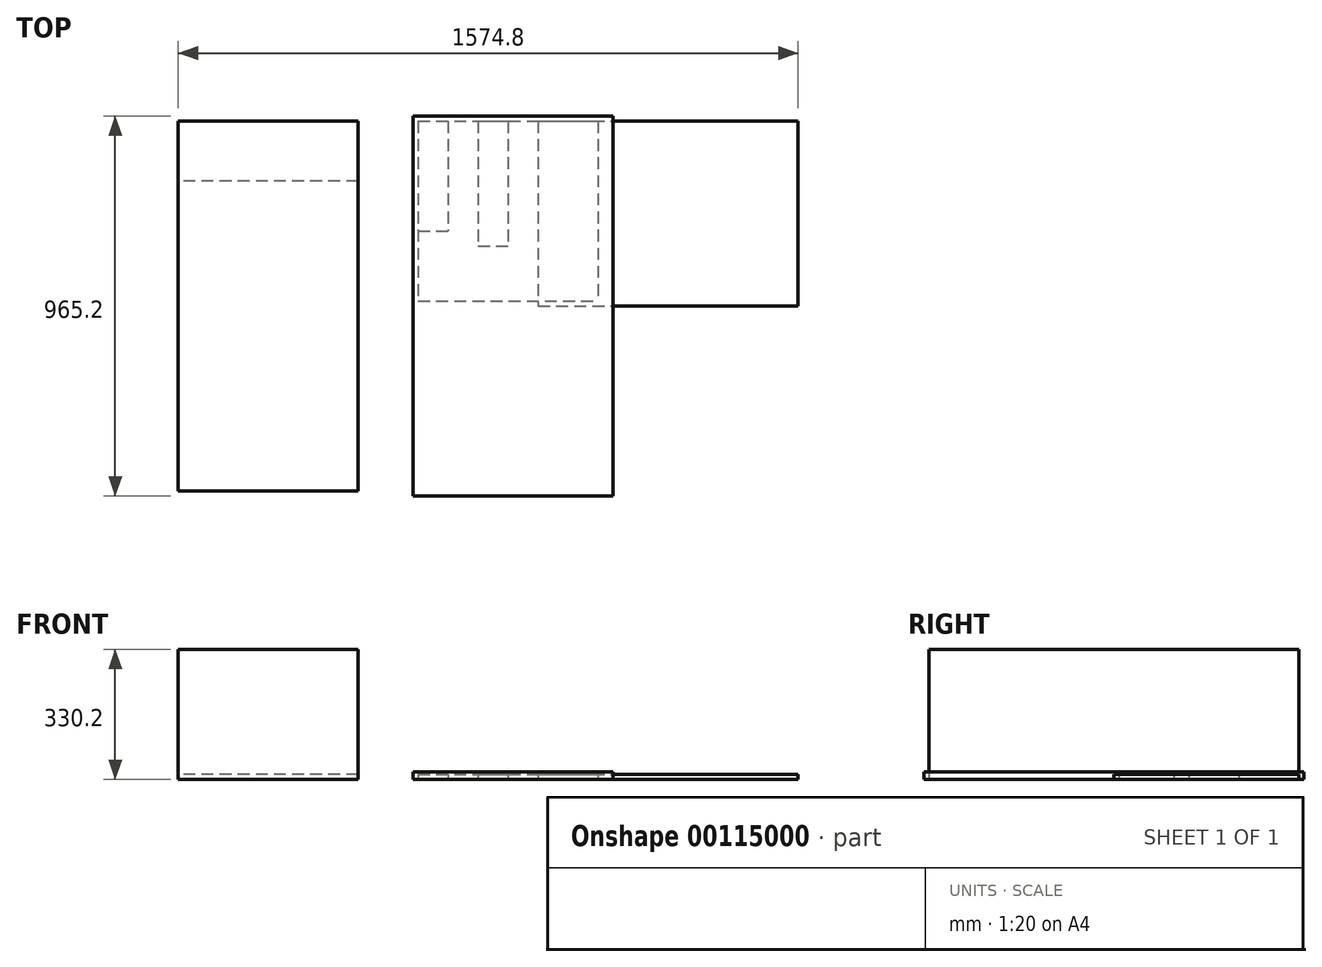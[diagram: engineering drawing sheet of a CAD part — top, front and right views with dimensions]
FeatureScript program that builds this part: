
annotation { "Feature Type Name" : "Feature", "Feature Type Description" : "" }
export const myFeature = defineFeature(function(context is Context, id is Id, definition is map)
    precondition{}
    {
        {
            var Q0;
            Q0=qCreatedBy(makeId("Top.planeOp"),FACE);
            var sketch = newSketch(context, id + "F0", { "sketchPlane" : qUnion([Q0])});
            skLineSegment(sketch, "E0.bottom", {"start": v(0, 0) * mm, "end": v(482.6, 0) * mm});
            skLineSegment(sketch, "E0.top", {"start": v(0, -939.8) * mm, "end": v(482.6, -939.8) * mm});
            skLineSegment(sketch, "E0.left", {"start": v(0, 0) * mm, "end": v(0, -939.8) * mm});
            skLineSegment(sketch, "E0.right", {"start": v(482.6, 0) * mm, "end": v(482.6, -939.8) * mm});
            skLineSegment(sketch, "E1.bottom", {"start": v(495.3, -952.5) * mm, "end": v(-12.7, -952.5) * mm});
            skLineSegment(sketch, "E1.top", {"start": v(495.3, 12.7) * mm, "end": v(-12.7, 12.7) * mm});
            skLineSegment(sketch, "E1.left", {"start": v(495.3, -952.5) * mm, "end": v(495.3, 12.7) * mm});
            skLineSegment(sketch, "E1.right", {"start": v(-12.7, -952.5) * mm, "end": v(-12.7, 12.7) * mm});
            skLineSegment(sketch, "E2", {"start": v(0, -939.8) * mm, "end": v(-12.7, -952.5) * mm});
            skLineSegment(sketch, "E3", {"start": v(-12.7, 12.7) * mm, "end": v(0, 0) * mm});
            skLineSegment(sketch, "E4", {"start": v(495.3, 12.7) * mm, "end": v(482.6, 0) * mm});
            skLineSegment(sketch, "E5", {"start": v(495.3, -952.5) * mm, "end": v(482.6, -939.8) * mm});
            skLineSegment(sketch, "E6.bottom", {"start": v(-152.4, 0) * mm, "end": v(-609.6, 0) * mm});
            skLineSegment(sketch, "E6.top", {"start": v(-152.4, -939.8) * mm, "end": v(-609.6, -939.8) * mm});
            skLineSegment(sketch, "E6.left", {"start": v(-152.4, 0) * mm, "end": v(-152.4, -939.8) * mm});
            skLineSegment(sketch, "E6.right", {"start": v(-609.6, 0) * mm, "end": v(-609.6, -939.8) * mm});
            skSolve(sketch);
        }
        {
            var Q0;
            Q0=qCreatedBy(makeId("Top.planeOp"),FACE);
            var sketch = newSketch(context, id + "F1", { "sketchPlane" : qUnion([Q0])});
            skLineSegment(sketch, "E7.bottom", {"start": v(0, 0) * mm, "end": v(76.2, 0) * mm});
            skLineSegment(sketch, "E7.top", {"start": v(0, -279.4) * mm, "end": v(76.2, -279.4) * mm});
            skLineSegment(sketch, "E7.left", {"start": v(0, 0) * mm, "end": v(0, -279.4) * mm});
            skLineSegment(sketch, "E7.right", {"start": v(76.2, 0) * mm, "end": v(76.2, -279.4) * mm});
            skLineSegment(sketch, "E8.bottom", {"start": v(152.4, 0) * mm, "end": v(228.6, 0) * mm});
            skLineSegment(sketch, "E8.top", {"start": v(152.4, -317.5) * mm, "end": v(228.6, -317.5) * mm});
            skLineSegment(sketch, "E8.left", {"start": v(152.4, 0) * mm, "end": v(152.4, -317.5) * mm});
            skLineSegment(sketch, "E8.right", {"start": v(228.6, 0) * mm, "end": v(228.6, -317.5) * mm});
            skLineSegment(sketch, "E9.bottom", {"start": v(304.8, 0) * mm, "end": v(965.2, 0) * mm});
            skLineSegment(sketch, "E9.top", {"start": v(304.8, -469.9) * mm, "end": v(965.2, -469.9) * mm});
            skLineSegment(sketch, "E9.left", {"start": v(304.8, 0) * mm, "end": v(304.8, -469.9) * mm});
            skLineSegment(sketch, "E9.right", {"start": v(965.2, 0) * mm, "end": v(965.2, -469.9) * mm});
            skPoint(sketch, "E10.centerSnap0", {"position": v(965.2, -234.95) * mm});
            skPoint(sketch, "E10.centerSnap1", {"position": v(635, 0) * mm});
            skSolve(sketch);
        }
        {
            var Q0;
            Q0=qCreatedBy(makeId("Top.planeOp"),FACE);
            var sketch = newSketch(context, id + "F2", { "sketchPlane" : qUnion([Q0])});
            skLineSegment(sketch, "E11.bottom", {"start": v(0, 0) * mm, "end": v(457.2, 0) * mm});
            skLineSegment(sketch, "E11.top", {"start": v(0, -457.2) * mm, "end": v(457.2, -457.2) * mm});
            skLineSegment(sketch, "E11.left", {"start": v(0, 0) * mm, "end": v(0, -457.2) * mm});
            skLineSegment(sketch, "E11.right", {"start": v(457.2, 0) * mm, "end": v(457.2, -457.2) * mm});
            skLineSegment(sketch, "E12.bottom", {"start": v(-152.4, 0) * mm, "end": v(-609.6, 0) * mm});
            skLineSegment(sketch, "E12.top", {"start": v(-152.4, -152.4) * mm, "end": v(-609.6, -152.4) * mm});
            skLineSegment(sketch, "E12.left", {"start": v(-152.4, 0) * mm, "end": v(-152.4, -152.4) * mm});
            skLineSegment(sketch, "E12.right", {"start": v(-609.6, 0) * mm, "end": v(-609.6, -152.4) * mm});
            skSolve(sketch);
        }
        {
            var Q0;
            Q0=makeQuery(id+"F0.imprint","IMPRINT",FACE,{"disambiguationData":[TD([[makeQuery(id+"F0.imprint","IMPRINT",EDGE,{"derivedFrom":sQuery(id+"F0.wireOp",EDGE,"E6.bottom")}),1.0]])]});
            extrude(context, id + "F3", {"entities" : qUnion([Q0]), "depth" : 330.2 * mm});
        }
        {
            var Q0;
            Q0=makeQuery(id+"F0.imprint","IMPRINT",FACE,{"disambiguationData":[TD([[makeQuery(id+"F0.imprint","IMPRINT",EDGE,{"derivedFrom":sQuery(id+"F0.wireOp",EDGE,"E0.right")}),1.0]])]});
            var Q1;
            Q1=makeQuery(id+"F0.imprint","IMPRINT",FACE,{"disambiguationData":[TD([[makeQuery(id+"F0.imprint","IMPRINT",EDGE,{"derivedFrom":sQuery(id+"F0.wireOp",EDGE,"E0.bottom")}),1.0]])]});
            var Q2;
            Q2=makeQuery(id+"F0.imprint","IMPRINT",FACE,{"disambiguationData":[TD([[makeQuery(id+"F0.imprint","IMPRINT",EDGE,{"derivedFrom":sQuery(id+"F0.wireOp",EDGE,"E0.bottom")}),-1.0]])]});
            var Q3;
            Q3=makeQuery(id+"F0.imprint","IMPRINT",FACE,{"disambiguationData":[TD([[makeQuery(id+"F0.imprint","IMPRINT",EDGE,{"derivedFrom":sQuery(id+"F0.wireOp",EDGE,"E0.left")}),-1.0]])]});
            var Q4;
            Q4=makeQuery(id+"F0.imprint","IMPRINT",FACE,{"disambiguationData":[TD([[makeQuery(id+"F0.imprint","IMPRINT",EDGE,{"derivedFrom":sQuery(id+"F0.wireOp",EDGE,"E0.top")}),-1.0]])]});
            extrude(context, id + "F4", {"entities" : qUnion([Q0, Q1, Q2, Q3, Q4]), "depth" : 19.05 * mm});
        }
        {
            var Q0;
            Q0=makeQuery(id+"F1.imprint","IMPRINT",FACE,{"disambiguationData":[TD([[makeQuery(id+"F1.imprint","IMPRINT",EDGE,{"derivedFrom":sQuery(id+"F1.wireOp",EDGE,"E9.bottom")}),-1.0]])]});
            var Q1;
            Q1=makeQuery(id+"F1.imprint","IMPRINT",FACE,{"disambiguationData":[TD([[makeQuery(id+"F1.imprint","IMPRINT",EDGE,{"derivedFrom":sQuery(id+"F1.wireOp",EDGE,"E8.bottom")}),-1.0]])]});
            var Q2;
            Q2=makeQuery(id+"F1.imprint","IMPRINT",FACE,{"disambiguationData":[TD([[makeQuery(id+"F1.imprint","IMPRINT",EDGE,{"derivedFrom":sQuery(id+"F1.wireOp",EDGE,"E7.bottom")}),-1.0]])]});
            extrude(context, id + "F5", {"entities" : qUnion([Q0, Q1, Q2]), "depth" : 12.7 * mm});
        }
        {
            var Q0;
            Q0=makeQuery(id+"F2.imprint","IMPRINT",FACE,{"disambiguationData":[TD([[makeQuery(id+"F2.imprint","IMPRINT",EDGE,{"derivedFrom":sQuery(id+"F2.wireOp",EDGE,"E12.bottom")}),1.0]])]});
            var Q1;
            Q1=makeQuery(id+"F2.imprint","IMPRINT",FACE,{"disambiguationData":[TD([[makeQuery(id+"F2.imprint","IMPRINT",EDGE,{"derivedFrom":sQuery(id+"F2.wireOp",EDGE,"E11.bottom")}),-1.0]])]});
            extrude(context, id + "F6", {"entities" : qUnion([Q0, Q1]), "depth" : 12.7 * mm});
        }
    });
